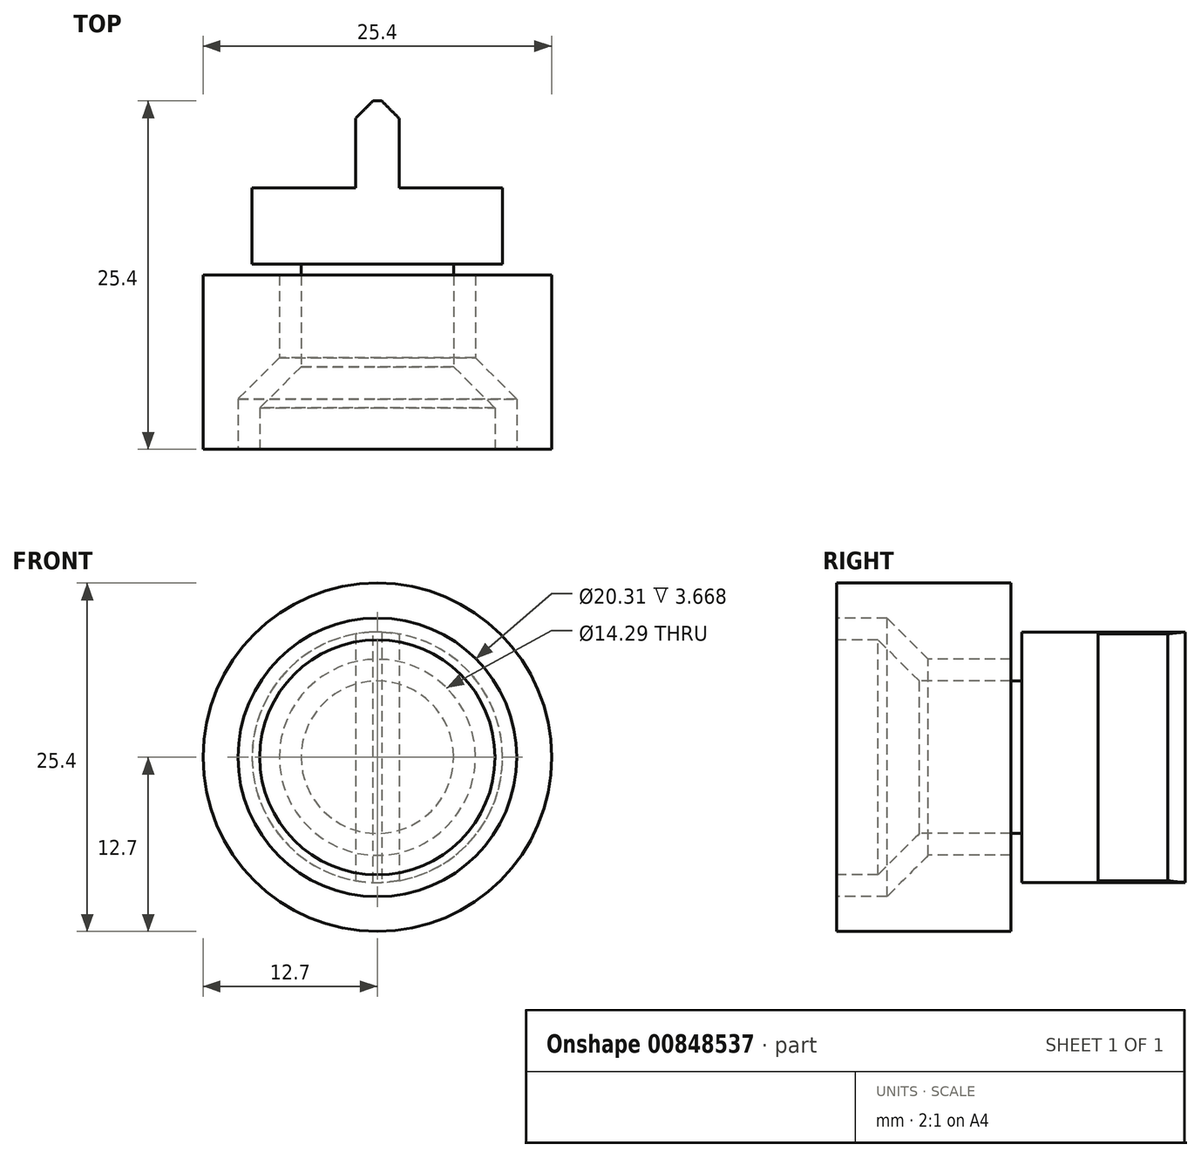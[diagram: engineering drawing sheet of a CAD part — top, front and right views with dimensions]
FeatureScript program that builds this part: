
annotation { "Feature Type Name" : "Feature", "Feature Type Description" : "" }
export const myFeature = defineFeature(function(context is Context, id is Id, definition is map)
    precondition{}
    {
        {
            var Q0;
            Q0=qCreatedBy(makeId("Top.planeOp"),FACE);
            var sketch = newSketch(context, id + "F0", { "sketchPlane" : qUnion([Q0])});
            skLineSegment(sketch, "E0.bottom", {"start": v(0, 0) * mm, "end": v(12.7, 0) * mm});
            skLineSegment(sketch, "E0.top", {"start": v(0, 12.7) * mm, "end": v(12.7, 12.7) * mm});
            skLineSegment(sketch, "E0.left", {"start": v(0, 0) * mm, "end": v(0, 12.7) * mm});
            skLineSegment(sketch, "E0.right", {"start": v(12.7, 0) * mm, "end": v(12.7, 12.7) * mm});
            skPoint(sketch, "E1.endSnap0", {"position": v(12.7, 6.35) * mm});
            skLineSegment(sketch, "E2.0", {"start": v(5.56, 6.02) * mm, "end": v(8.57, 3.01) * mm});
            skLineSegment(sketch, "E2.1", {"start": v(5.56, 13.5) * mm, "end": v(5.56, 6.02) * mm});
            skLineSegment(sketch, "E3.0", {"start": v(0, 19.05) * mm, "end": v(9.13, 19.05) * mm});
            skLineSegment(sketch, "E4.0", {"start": v(5.56, 13.5) * mm, "end": v(9.13, 13.5) * mm});
            skLineSegment(sketch, "E5", {"start": v(0, 19.05) * mm, "end": v(0, 12.7) * mm});
            skLineSegment(sketch, "E6", {"start": v(9.13, 13.5) * mm, "end": v(9.13, 19.05) * mm});
            skPoint(sketch, "E7.orphan", {"position": v(12.7, 13.5) * mm});
            skLineSegment(sketch, "E8.0", {"start": v(7.14, 13.5) * mm, "end": v(7.14, 6.68) * mm});
            skLineSegment(sketch, "E9.0", {"start": v(7.14, 6.68) * mm, "end": v(10.15, 3.67) * mm});
            skLineSegment(sketch, "E10", {"start": v(8.57, 3.01) * mm, "end": v(8.57, 0) * mm});
            skPoint(sketch, "E11.orphan", {"position": v(11.58, 0) * mm});
            skLineSegment(sketch, "E12.0", {"start": v(10.15, 3.67) * mm, "end": v(10.15, 0) * mm});
            skSolve(sketch);
        }
        {
            var Q0;
            {var subQ0=sQuery(id+"F0.wireOp",EDGE,"E0.right");Q0=makeQuery(id+"F0.imprint","IMPRINT",FACE,{"disambiguationData":[TD([[makeQuery(id+"F0.imprint","IMPRINT",EDGE,{"derivedFrom":subQ0}),1.0]])]});}
            var Q1;
            {var subQ1=sQuery(id+"F0.wireOp",EDGE,"E0.left");Q1=makeQuery(id+"F0.imprint","IMPRINT",FACE,{"disambiguationData":[TD([[makeQuery(id+"F0.imprint","IMPRINT",EDGE,{"derivedFrom":subQ1}),-1.0]])]});}
            var Q2;
            Q2=makeQuery(id+"F0.imprint","IMPRINT",FACE,{"disambiguationData":[TD([[makeQuery(id+"F0.imprint","IMPRINT",EDGE,{"derivedFrom":sQuery(id+"F0.wireOp",EDGE,"E3.0")}),-1.0]])]});
            var Q3;
            Q3=sQuery(id+"F0.wireOp",EDGE,"E0.left");
            revolve(context, id + "F1", {"surfaceOperationType" : NewSurfaceOperationType.NEW, "entities" : qUnion([Q0, Q1, Q2]), "axis" : qUnion([Q3]), "revolveType" : RevolveType.FULL});
        }
        {
            var Q0;
            Q0=makeQuery(id+"F1.opRevolve","SWEPT_FACE",FACE,{"disambiguationData":[OSD([sQuery(id+"F0.wireOp",EDGE,"E3.0")])]});
            var sketch = newSketch(context, id + "F2", { "sketchPlane" : qUnion([Q0])});
            skLineSegment(sketch, "E13.0", {"start": v(-0.8, 9.1) * mm, "end": v(-0.8, -9.1) * mm});
            skLineSegment(sketch, "E14.MirrorCS", {"start": v(0.8, 9.1) * mm, "end": v(0.8, -9.1) * mm});
            skCircle(sketch, "E15", {"center": v(0, 0) * mm, "radius": 9.13 * mm});
            skPoint(sketch, "E16.orphan", {"position": v(-0.8, -9.13) * mm});
            skPoint(sketch, "E17.orphan", {"position": v(0.8, -9.13) * mm});
            skPoint(sketch, "E18.orphan", {"position": v(0.8, 0) * mm});
            skPoint(sketch, "E19.orphan", {"position": v(-0.8, 0) * mm});
            skLineSegment(sketch, "E20.0", {"start": v(-1.59, 8.99) * mm, "end": v(-1.59, -8.99) * mm});
            skLineSegment(sketch, "E21.MirrorCS", {"start": v(1.59, 8.99) * mm, "end": v(1.59, -8.99) * mm});
            skSolve(sketch);
        }
        {
            var Q0;
            {var subQ0=sQuery(id+"F2.wireOp",EDGE,"E14.MirrorCS");Q0=makeQuery(id+"F2.imprint","IMPRINT",FACE,{"disambiguationData":[TD([[makeQuery(id+"F2.imprint","IMPRINT",EDGE,{"derivedFrom":subQ0}),1.0]])]});}
            var Q1;
            {var subQ0=sQuery(id+"F2.wireOp",EDGE,"E13.0");Q1=makeQuery(id+"F2.imprint","IMPRINT",FACE,{"disambiguationData":[TD([[makeQuery(id+"F2.imprint","IMPRINT",EDGE,{"derivedFrom":subQ0}),-1.0]])]});}
            var Q2;
            {var subQ0=sQuery(id+"F2.wireOp",EDGE,"E13.0");Q2=makeQuery(id+"F2.imprint","IMPRINT",FACE,{"disambiguationData":[TD([[makeQuery(id+"F2.imprint","IMPRINT",EDGE,{"derivedFrom":subQ0}),1.0]])]});}
            extrude(context, id + "F3", {"entities" : qUnion([Q0, Q1, Q2]), "operationType" : NewBodyOperationType.ADD, "depth" : 6.35 * mm, "offsetDistance" : 25.4 * mm});
        }
        {
            var Q0;
            Q0=makeQuery(id+"F3.opExtrude","CAP_EDGE",EDGE,{"disambiguationData":[OSD([sQuery(id+"F2.wireOp",EDGE,"E21.MirrorCS")])],"isStart":false});
            var Q1;
            Q1=makeQuery(id+"F3.opExtrude","CAP_EDGE",EDGE,{"disambiguationData":[OSD([sQuery(id+"F2.wireOp",EDGE,"E20.0")])],"isStart":false});
            chamfer(context, id + "F4", {"entities" : qUnion([Q0, Q1]), "width" : 1.27 * mm, "tangentPropagation" : true});
        }
    });
